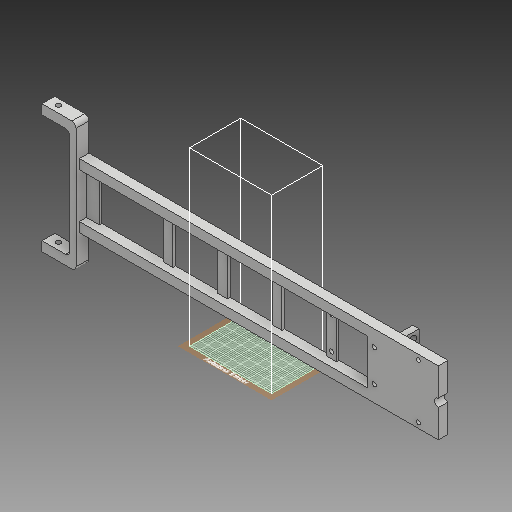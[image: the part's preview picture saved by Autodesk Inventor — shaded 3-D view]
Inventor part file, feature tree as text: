
AUTODESK INVENTOR PART (.ipt)
format: ipt  version: 2018 (Build 220112000, 112)  size: 913,920 bytes
history: native  units: mm
features: sketch x64, extrude x49, fillet x13, hole x6, plane x1
ambient origin geometry x8: Origin, YZ Plane, XZ Plane, XY Plane, X Axis, Y Axis, Z Axis, Center Point
bodies: Solid1 (feature_tree)
feature tree (133):
  extrude  "Extrusion1"  Depth=50.0mm
  hole  "Hole1"  [1 undecoded]
  hole  "Hole2"  [1 undecoded]
  extrude  "Extrusion2"  Depth=25.0mm
  extrude  "Extrusion3"  Depth=25.0mm
  extrude  "Extrusion4"  Depth=5.0mm
  sketch  "Sketch7"  dims[d25=10.0mm d26=5.0mm]
  extrude  "Extrusion5"  Depth=5.0mm
  extrude  "Extrusion6"  Depth=35.0mm
  extrude  "Extrusion7"  Depth=35.0mm
  extrude  "Extrusion8"  Depth=35.0mm
  extrude  "Extrusion9"  Depth=2.0mm TaperAngle=0.0deg
  extrude  "Extrusion10"  Depth=7.5mm TaperAngle=0.0deg
  extrude  "Extrusion11"  Depth=10.0mm
  extrude  "Extrusion12"  Depth=7.5mm
  fillet  "Fillet1"  Radius=7.5mm
  fillet  "Fillet2"  Radius=25.0mm
  fillet  "Fillet3"  Radius=3.0mm
  fillet  "Fillet4"  Radius=3.2mm
  fillet  "Fillet5"  Radius=2.1mm
  fillet  "Fillet6"  Radius=5.5mm
  extrude  "Extrusion13"  Depth=92.5mm TaperAngle=0.0deg
  sketch  "Sketch17"  dims[d58=4.25mm d59=241.0mm d60=0.0mm]
  hole  "Hole3"  [1 undecoded]
  hole  "Hole4"  [1 undecoded]
  extrude  "Extrusion14"  Depth=5.0mm
  extrude  "Extrusion15"  Depth=2.5mm TaperAngle=0.0deg
  extrude  "Extrusion16"  Depth=6.35mm
  extrude  "Extrusion17"  Depth=2.5mm
  extrude  "Extrusion18"  Depth=14.55mm TaperAngle=0.0deg
  extrude  "Extrusion19"  Depth=0.1mm
  extrude  "Extrusion20"  Depth=3.25mm
  extrude  "Extrusion21"  Depth=3.25mm
  hole  "Hole5"  [1 undecoded]
  extrude  "Extrusion22"  Depth=2.0mm
  extrude  "Extrusion23"  Depth=15.0mm
  extrude  "Extrusion24"  Depth=10.0mm TaperAngle=0.0deg
  hole  "Hole6"  [1 undecoded]
  extrude  "Extrusion25"  Depth=100.0mm TaperAngle=0.0deg
  extrude  "Extrusion26"  Depth=2.0mm TaperAngle=0.0deg
  sketch  "Sketch35"  dims[d116=3.3mm d117=3.3mm]
  plane  "Work Plane1"
  sketch  "Sketch36"  dims[d118=3.3mm d119=3.3mm d120=2.0mm d121=0.0mm]
  extrude  "Extrusion27"  Depth=3.3mm
  extrude  "Extrusion28"  Depth=2.0mm
  fillet  "Fillet7"  Radius=2.0mm
  extrude  "Extrusion29"  Depth=8.0mm
  extrude  "Extrusion30"  Depth=21.0mm
  extrude  "Extrusion31"  Depth=8.5mm
  extrude  "Extrusion32"  Depth=3.5mm
  sketch  "Sketch43"  dims[d142=10.0mm d143=0.0mm d144=7.5mm d145=0.0mm]
  fillet  "Fillet8"  Radius=3.3mm
  extrude  "Extrusion33"  Depth=3.3mm
  extrude  "Extrusion34"  Depth=7.5mm TaperAngle=0.0deg
  extrude  "Extrusion35"  Depth=15.0mm
  extrude  "Extrusion36"  Depth=100.0mm TaperAngle=0.0deg
  extrude  "Extrusion37"  Depth=5.0mm
  fillet  "Fillet9"  Radius=5.0mm
  fillet  "Fillet10"  Radius=37.5mm
  fillet  "Fillet11"  Radius=1.1mm
  fillet  "Fillet12"  Radius=37.5mm
  sketch  "Sketch49"  dims[d170=5.5mm d171=0.0mm d172=10.0mm d173=0.0mm]
  extrude  "Extrusion38"  Depth=3.0mm
  extrude  "Extrusion39"  Depth=10.0mm TaperAngle=0.0deg
  extrude  "Extrusion40"  Depth=74.724mm
  fillet  "Fillet13"  Radius=85.515mm
  extrude  "Extrusion41"  Depth=5.0mm
  extrude  "Extrusion42"  Depth=5.0mm
  sketch  "Sketch55"  dims[d186=10.0mm d187=2.0mm d188=0.0mm]
  extrude  "Extrusion43"  Depth=5.0mm
  extrude  "Extrusion44"  Depth=2.0mm TaperAngle=0.0deg
  sketch  "Sketch58"  dims[d195=1.0mm d196=0.0mm d197=20.0mm]
  extrude  "Extrusion45"  Depth=2.0mm TaperAngle=0.0deg
  extrude  "Extrusion46"  Depth=1.0mm TaperAngle=0.0deg
  sketch  "Sketch61"  dims[d202=2.5mm d203=0.0mm]
  extrude  "Extrusion47"  Depth=10.0mm
  extrude  "Extrusion48"  Depth=20.0mm
  extrude  "Extrusion49"  Depth=7.5mm
  sketch  "Sketch1"  dims[d0=50.0mm d1=50.0mm]
  sketch  "Sketch2"  dims[d2=240.0mm d3=7.5mm]
  sketch  "Sketch3"  dims[d4=7.5mm d5=7.5mm d6=0.0mm]
  sketch  "Sketch4"  dims[d7=6.35mm d8=6.0mm d9=4.0mm d10=2.0mm d11=90.0deg d12=8.0mm d13=20.594885mm d14=25.0mm]
  sketch  "Sketch5"  dims[d15=3.3mm d16=6.0mm d17=4.0mm d18=2.0mm d19=90.0deg d20=8.0mm d21=20.594885mm d22=25.0mm]
  sketch  "Sketch6"  dims[d23=180.0deg d24=5.0mm]
  sketch  "Sketch8"  dims[d27=17.5mm d28=0.0mm d30=35.0mm]
  sketch  "Sketch9"  dims[d31=35.0mm d32=35.0mm]
  sketch  "Sketch10"  dims[d33=35.0mm d34=35.0mm]
  sketch  "Sketch11"  dims[d35=35.0mm d36=2.0mm d37=0.0mm]
  sketch  "Sketch12"  dims[d38=10.0mm d39=7.5mm d40=0.0mm]
  sketch  "Sketch13"  dims[d41=100.0mm d42=10.0mm]
  sketch  "Sketch14"  dims[d43=7.5mm d44=0.0mm d45=7.5mm d46=7.5mm d47=25.0mm d48=0.0mm d49=3.0mm d50=3.2mm d51=2.1mm d52=5.5mm]
  sketch  "Sketch15"  dims[d53=3.3mm d54=92.5mm d55=0.0mm]
  sketch  "Sketch16"  dims[d56=5.5mm d57=3.3mm]
  sketch  "Sketch18"  dims[d61=4.44mm d62=5.0mm]
  sketch  "Sketch19"  dims[d63=2.5mm d64=91.25mm d65=0.0mm]
  sketch  "Sketch20"  dims[d66=30.0mm d67=6.35mm]
  sketch  "Sketch21"  dims[d68=3.8mm d69=0.0mm d70=2.5mm]
  sketch  "Sketch22"  dims[d71=14.55mm d72=0.0mm d73=14.55mm d74=0.0mm]
  sketch  "Sketch23"  dims[d75=0.1mm d76=0.1mm]
  sketch  "Sketch24"  dims[d77=3.25mm d78=3.25mm]
  sketch  "Sketch25"  dims[d79=3.25mm d80=3.25mm]
  sketch  "Sketch26"  dims[d81=35.0mm d82=10.0mm]
  sketch  "Sketch27"  dims[d83=2.0mm d84=0.0mm d85=3.6mm]
  sketch  "Sketch28"  dims[d86=3.6mm]
  sketch  "Sketch29"  dims[d87=3.3mm d88=6.0mm d89=4.0mm d90=2.0mm d91=90.0deg d92=15.0mm d93=20.594885mm]
  sketch  "Sketch30"  dims[d94=3.3mm d95=6.0mm d96=4.0mm d97=2.0mm d98=90.0deg d99=15.0mm d100=20.594885mm d101=6.0mm]
  sketch  "Sketch31"  dims[d102=20.0mm d103=0.0mm d104=10.0mm d105=0.0mm]
  sketch  "Sketch32"  dims[d106=2.0mm d107=0.0mm d108=4.0mm]
  sketch  "Sketch33"  dims[d109=100.0mm d110=0.0mm d111=100.0mm d112=0.0mm]
  sketch  "Sketch34"  dims[d113=5.0mm d114=2.0mm d115=0.0mm]
  sketch  "Sketch37"  dims[d122=5.5mm d123=0.0mm]
  sketch  "Sketch38"  dims[d124=3.3mm d125=6.0mm d126=4.0mm d127=2.0mm d128=90.0deg d129=8.0mm d130=20.594885mm d131=42.0mm]
  sketch  "Sketch39"  dims[d132=17.0mm d133=21.0mm]
  sketch  "Sketch40"  dims[d135=8.5mm d136=15.825mm]
  sketch  "Sketch41"  dims[d137=3.5mm d138=21.0mm d139=3.3mm]
  sketch  "Sketch42"  dims[d140=3.3mm d141=3.3mm]
  sketch  "Sketch44"  dims[d146=100.0mm d147=0.0mm]
  sketch  "Sketch45"  dims[d148=5.0mm d149=6.0mm d150=4.0mm d151=2.0mm d152=90.0deg d153=15.0mm d154=0.0mm d155=3.75mm]
  sketch  "Sketch46"  dims[d156=100.0mm d157=0.0mm d158=100.0mm d159=0.0mm]
  sketch  "Sketch47"  dims[d160=-0.698132mm d161=5.0mm d162=5.0mm d163=37.5mm d164=0.0mm d165=1.1mm d166=37.5mm d167=0.0mm]
  sketch  "Sketch48"  dims[d168=0.2mm d169=3.0mm]
  sketch  "Sketch50"  dims[d174=74.724mm d175=74.724mm d176=85.515mm]
  sketch  "Sketch51"  dims[d177=5.0mm d178=85.515mm]
  sketch  "Sketch52"  dims[d179=5.0mm d180=85.515mm]
  sketch  "Sketch53"  dims[d181=5.0mm d182=85.515mm]
  sketch  "Sketch54"  dims[d183=5.0mm d184=2.0mm d185=0.0mm]
  sketch  "Sketch56"  dims[d189=2.0mm d190=1.0mm d191=0.0mm]
  sketch  "Sketch57"  dims[d192=2.0mm d193=0.0mm d194=10.0mm]
  sketch  "Sketch59"  dims[d198=1.0mm d199=0.0mm d200=7.5mm]
  sketch  "Sketch60"  dims[d201=5.0mm]
  sketch  "Sketch62"  dims[d204=3.25mm]
  sketch  "Sketch63"  dims[d205=3.25mm]
  sketch  "Sketch64"  dims[d206=3.25mm d207=3.25mm d208=6.25mm d209=9.58mm d210=250.0mm d211=0.0mm d212=5.25mm d213=4.3mm d214=0.0mm d215=4.3mm d216=0.0mm d217=0.25mm d218=9.7mm d219=100.0mm d220=0.0mm d221=9.8mm d222=4.5mm d223=4.3mm d224=0.0mm d225=9.8mm d226=4.3mm d227=0.0mm d228=10.0mm d229=0.0mm d230=20.0mm d231=10.0mm d232=0.0mm d233=5.0mm d234=5.0mm d235=10.0mm d236=0.0mm d237=3.65mm d238=7.5mm d239=0.0mm d240=7.5mm d241=0.0mm d242=50.0mm d243=0.0mm]
note: 6 required parameter values undecoded (feature->parameter linkage not recoverable at this tier; creation-order binding heuristic only, values carry confidence <= 0.55)
